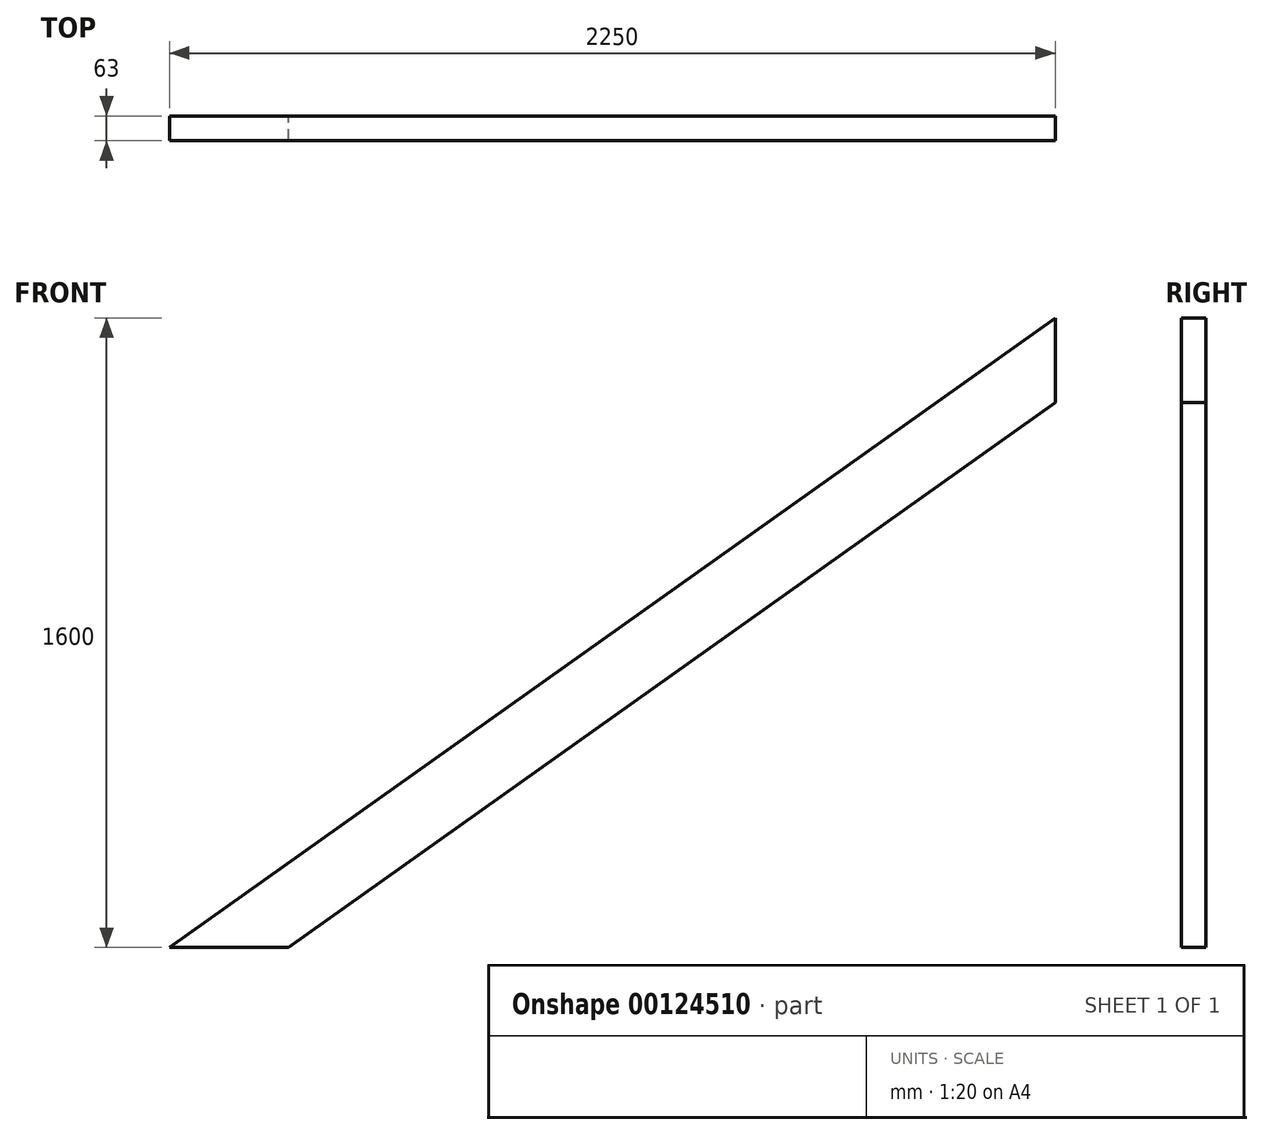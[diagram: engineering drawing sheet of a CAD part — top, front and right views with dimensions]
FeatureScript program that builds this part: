
annotation { "Feature Type Name" : "Feature", "Feature Type Description" : "" }
export const myFeature = defineFeature(function(context is Context, id is Id, definition is map)
    precondition{}
    {
        {
            var Q0;
            Q0=qCreatedBy(makeId("Front.planeOp"),FACE);
            var sketch = newSketch(context, id + "F0", { "sketchPlane" : qUnion([Q0])});
            skLineSegment(sketch, "E0", {"start": v(-644.12, 0) * mm, "end": v(-342.15, 0) * mm});
            skLineSegment(sketch, "E1", {"start": v(-342.15, 0) * mm, "end": v(1605.88, 1385.26) * mm});
            skLineSegment(sketch, "E2", {"start": v(1605.88, 1385.26) * mm, "end": v(1605.88, 1600) * mm});
            skLineSegment(sketch, "E3", {"start": v(1605.88, 1600) * mm, "end": v(-644.12, 0) * mm});
            skSolve(sketch);
        }
        {
            var Q0;
            Q0 = qSketchRegion(id + "F0", true);
            extrude(context, id + "F1", {"entities" : qUnion([Q0]), "depth" : 63 * mm});
        }
    });
